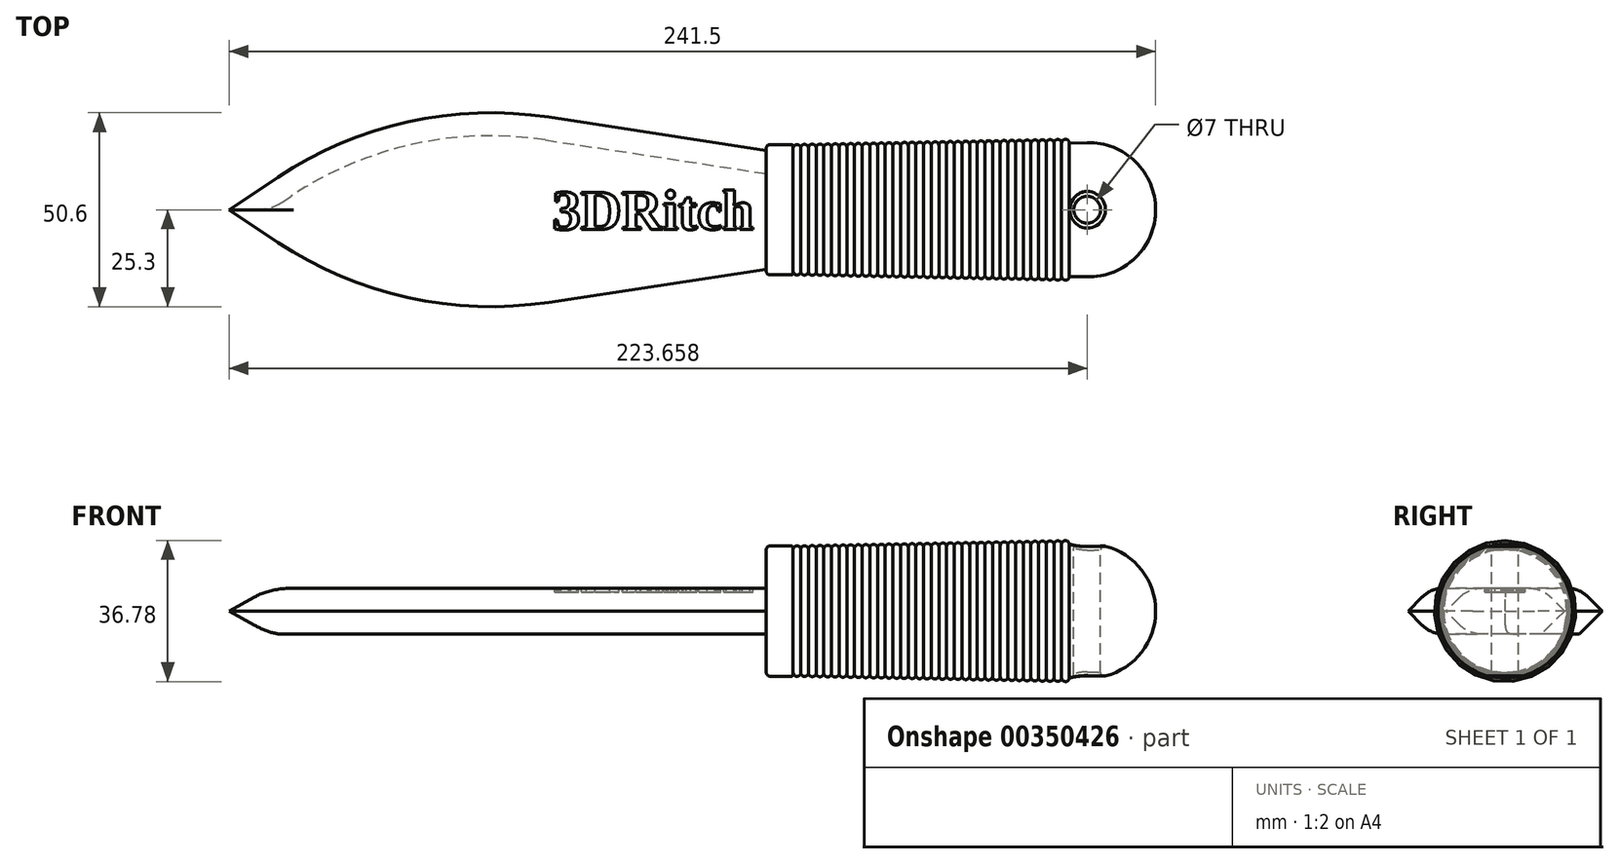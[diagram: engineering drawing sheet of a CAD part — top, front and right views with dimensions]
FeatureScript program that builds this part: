
annotation { "Feature Type Name" : "Feature", "Feature Type Description" : "" }
export const myFeature = defineFeature(function(context is Context, id is Id, definition is map)
    precondition{}
    {
        {
            var Q0;
            Q0=qCreatedBy(makeId("Top.planeOp"),FACE);
            var sketch = newSketch(context, id + "F0", { "sketchPlane" : qUnion([Q0])});
            skLineSegment(sketch, "E0", {"start": v(0, 0) * mm, "end": v(0, -16) * mm});
            skLineSegment(sketch, "E1", {"start": v(1, -17) * mm, "end": v(6.5, -17) * mm});
            skLineSegment(sketch, "E2", {"start": v(7, -16.5) * mm, "end": v(7, -16) * mm});
            skArc(sketch, "E3", {"start": v(83.66, -17.5) * mm, "mid": v(96.25, -12.5) * mm, "end": v(101.5, 0) * mm});
            skLineSegment(sketch, "E4", {"start": v(0, 0) * mm, "end": v(84, 0) * mm, "construction": true});
            skLineSegment(sketch, "E5", {"start": v(7, -16) * mm, "end": v(83.66, -17.5) * mm, "construction": true});
            skLineSegment(sketch, "E6", {"start": v(84, 0) * mm, "end": v(108.75, 0) * mm, "construction": true});
            skArc(sketch, "E7", {"start": v(7, -16) * mm, "mid": v(7.98, -17.02) * mm, "end": v(9, -16.04) * mm});
            skArc(sketch, "E8", {"start": v(9, -16.04) * mm, "mid": v(9.98, -17.06) * mm, "end": v(11, -16.08) * mm});
            skArc(sketch, "E9", {"start": v(13, -16.12) * mm, "mid": v(13.98, -17.14) * mm, "end": v(15, -16.16) * mm});
            skArc(sketch, "E10", {"start": v(15, -16.16) * mm, "mid": v(15.98, -17.18) * mm, "end": v(17, -16.2) * mm});
            skArc(sketch, "E11", {"start": v(17, -16.2) * mm, "mid": v(17.98, -17.21) * mm, "end": v(19, -16.23) * mm});
            skArc(sketch, "E12", {"start": v(19, -16.23) * mm, "mid": v(19.98, -17.25) * mm, "end": v(21, -16.27) * mm});
            skArc(sketch, "E13", {"start": v(21, -16.27) * mm, "mid": v(21.98, -17.3) * mm, "end": v(23, -16.31) * mm});
            skArc(sketch, "E14", {"start": v(11, -16.08) * mm, "mid": v(11.98, -17.1) * mm, "end": v(13, -16.12) * mm});
            skArc(sketch, "E15", {"start": v(23, -16.31) * mm, "mid": v(23.98, -17.33) * mm, "end": v(25, -16.35) * mm});
            skArc(sketch, "E16", {"start": v(25, -16.35) * mm, "mid": v(25.98, -17.37) * mm, "end": v(27, -16.4) * mm});
            skArc(sketch, "E17", {"start": v(27, -16.4) * mm, "mid": v(27.98, -17.4) * mm, "end": v(29, -16.43) * mm});
            skArc(sketch, "E18", {"start": v(31, -16.47) * mm, "mid": v(31.98, -17.49) * mm, "end": v(33, -16.5) * mm});
            skArc(sketch, "E19", {"start": v(35, -16.55) * mm, "mid": v(35.97, -17.57) * mm, "end": v(37, -16.59) * mm});
            skArc(sketch, "E20", {"start": v(37, -16.59) * mm, "mid": v(37.97, -17.6) * mm, "end": v(39, -16.62) * mm});
            skArc(sketch, "E21", {"start": v(39, -16.62) * mm, "mid": v(39.97, -17.64) * mm, "end": v(41, -16.66) * mm});
            skArc(sketch, "E22", {"start": v(41, -16.66) * mm, "mid": v(41.97, -17.68) * mm, "end": v(43, -16.7) * mm});
            skArc(sketch, "E23", {"start": v(43, -16.7) * mm, "mid": v(43.97, -17.72) * mm, "end": v(45, -16.74) * mm});
            skArc(sketch, "E24", {"start": v(29, -16.43) * mm, "mid": v(29.98, -17.45) * mm, "end": v(31, -16.47) * mm});
            skArc(sketch, "E25", {"start": v(33, -16.5) * mm, "mid": v(33.98, -17.53) * mm, "end": v(35, -16.55) * mm});
            skArc(sketch, "E26", {"start": v(45, -16.74) * mm, "mid": v(45.97, -17.76) * mm, "end": v(47, -16.78) * mm});
            skArc(sketch, "E27", {"start": v(47, -16.78) * mm, "mid": v(47.97, -17.8) * mm, "end": v(49, -16.82) * mm});
            skArc(sketch, "E28", {"start": v(49, -16.82) * mm, "mid": v(49.97, -17.84) * mm, "end": v(51, -16.86) * mm});
            skArc(sketch, "E29", {"start": v(51, -16.86) * mm, "mid": v(51.97, -17.88) * mm, "end": v(53, -16.9) * mm});
            skArc(sketch, "E30", {"start": v(53, -16.9) * mm, "mid": v(53.97, -17.92) * mm, "end": v(55, -16.94) * mm});
            skArc(sketch, "E31", {"start": v(55, -16.94) * mm, "mid": v(55.97, -17.96) * mm, "end": v(57, -16.98) * mm});
            skArc(sketch, "E32", {"start": v(57, -16.98) * mm, "mid": v(57.97, -18) * mm, "end": v(59, -17.02) * mm});
            skArc(sketch, "E33", {"start": v(59, -17.02) * mm, "mid": v(59.97, -18.03) * mm, "end": v(60.99, -17.05) * mm});
            skArc(sketch, "E34", {"start": v(60.99, -17.05) * mm, "mid": v(61.97, -18.07) * mm, "end": v(62.99, -17.1) * mm});
            skArc(sketch, "E35", {"start": v(62.99, -17.1) * mm, "mid": v(63.97, -18.11) * mm, "end": v(64.99, -17.13) * mm});
            skArc(sketch, "E36", {"start": v(64.99, -17.13) * mm, "mid": v(65.97, -18.15) * mm, "end": v(66.99, -17.17) * mm});
            skArc(sketch, "E37", {"start": v(66.99, -17.17) * mm, "mid": v(67.97, -18.2) * mm, "end": v(68.99, -17.21) * mm});
            skArc(sketch, "E38", {"start": v(68.99, -17.21) * mm, "mid": v(69.97, -18.23) * mm, "end": v(70.99, -17.25) * mm});
            skArc(sketch, "E39", {"start": v(70.99, -17.25) * mm, "mid": v(71.97, -18.27) * mm, "end": v(72.99, -17.29) * mm});
            skArc(sketch, "E40", {"start": v(72.99, -17.29) * mm, "mid": v(73.97, -18.3) * mm, "end": v(74.99, -17.33) * mm});
            skArc(sketch, "E41", {"start": v(74.99, -17.33) * mm, "mid": v(75.97, -18.35) * mm, "end": v(76.99, -17.37) * mm});
            skArc(sketch, "E42", {"start": v(76.99, -17.37) * mm, "mid": v(77.97, -18.39) * mm, "end": v(78.99, -17.4) * mm});
            skLineSegment(sketch, "E43", {"start": v(78.99, -17.4) * mm, "end": v(83.66, -17.5) * mm});
            skPoint(sketch, "E44.visualSharp", {"position": v(0, -17) * mm});
            skArc(sketch, "E44.filletArc", {"start": v(0, -16) * mm, "mid": v(0.3, -16.7) * mm, "end": v(1, -17) * mm});
            skPoint(sketch, "E45.visualSharp", {"position": v(7, -17) * mm});
            skArc(sketch, "E45.filletArc", {"start": v(6.5, -17) * mm, "mid": v(6.85, -16.85) * mm, "end": v(7, -16.5) * mm});
            skLineSegment(sketch, "E46", {"start": v(0, 0) * mm, "end": v(101.5, 0) * mm});
            skSolve(sketch);
        }
        {
            var Q0;
            Q0 = qSketchRegion(id + "F0", true);
            var Q1;
            Q1=sQuery(id+"F0.wireOp",EDGE,"E4");
            revolve(context, id + "F1", {"entities" : qUnion([Q0]), "axis" : qUnion([Q1]), "revolveType" : RevolveType.FULL});
        }
        {
            var Q0;
            Q0=qCreatedBy(makeId("Top.planeOp"),FACE);
            var sketch = newSketch(context, id + "F2", { "sketchPlane" : qUnion([Q0])});
            skLineSegment(sketch, "E47", {"start": v(0, 15.5) * mm, "end": v(0, -15.5) * mm});
            skLineSegment(sketch, "E48", {"start": v(0, 15.5) * mm, "end": v(-95, 30) * mm});
            skLineSegment(sketch, "E49", {"start": v(-95, 30) * mm, "end": v(-140, 0) * mm});
            skLineSegment(sketch, "E50", {"start": v(-140, 0) * mm, "end": v(-95, -30) * mm});
            skLineSegment(sketch, "E51", {"start": v(-95, -30) * mm, "end": v(0, -15.5) * mm});
            skLineSegment(sketch, "E52", {"start": v(-95, 30) * mm, "end": v(-95, 0) * mm, "construction": true});
            skLineSegment(sketch, "E53", {"start": v(-95, 0) * mm, "end": v(-95, -30) * mm, "construction": true});
            skSolve(sketch);
        }
        {
            var Q0;
            Q0 = qSketchRegion(id + "F2", true);
            extrude(context, id + "F3", {"entities" : qUnion([Q0]), "operationType" : NewBodyOperationType.ADD, "endBound" : BoundingType.SYMMETRIC, "depth" : 12 * mm});
        }
        {
            var Q0;
            Q0=makeQuery(id+"F3.opExtrude","SWEPT_EDGE",EDGE,{"disambiguationData":[OSD([sQuery(id+"F2.wireOp",EDGE,"E48"),sQuery(id+"F2.wireOp",EDGE,"E49")])]});
            var Q1;
            Q1=makeQuery(id+"F3.opExtrude","SWEPT_EDGE",EDGE,{"disambiguationData":[OSD([sQuery(id+"F2.wireOp",EDGE,"E50"),sQuery(id+"F2.wireOp",EDGE,"E51")])]});
            fillet(context, id + "F4", {"entities" : qUnion([Q0, Q1]), "radius" : 100 * mm, "tangentPropagation" : true, "allowEdgeOverflow" : false});
        }
        {
            var Q0;
            Q0=makeQuery(id+"F3.opExtrude","CAP_EDGE",EDGE,{"disambiguationData":[OSD([sQuery(id+"F2.wireOp",EDGE,"E49")])],"isStart":false});
            var Q1;
            Q1=makeQuery(id+"F3.opExtrude","CAP_EDGE",EDGE,{"disambiguationData":[OSD([sQuery(id+"F2.wireOp",EDGE,"E49")])],"isStart":true});
            var Q2;
            {var subQ0=sQuery(id+"F2.wireOp",EDGE,"E51");var subQ1=sQuery(id+"F2.wireOp",EDGE,"E50");Q2=makeQuery(id+"F4.opFillet","BLEND_EDGE",EDGE,{"blendedFrom":[makeQuery(id+"F3.opExtrude","SWEPT_EDGE",EDGE,{"disambiguationData":[OSD([subQ1,subQ0])]}),makeQuery(id+"F3.opExtrude","CAP_FACE",FACE,{"disambiguationData":[OSD([sQuery(id+"F2.wireOp",EDGE,"E47"),sQuery(id+"F2.wireOp",EDGE,"E48"),sQuery(id+"F2.wireOp",EDGE,"E49"),subQ1,subQ0])],"isStart":false})],"blendedInto":[makeQuery(id+"F3.opExtrude","CAP_FACE",FACE,{"disambiguationData":[OSD([sQuery(id+"F2.wireOp",EDGE,"E47"),sQuery(id+"F2.wireOp",EDGE,"E48"),sQuery(id+"F2.wireOp",EDGE,"E49"),subQ1,subQ0])],"isStart":false})]});}
            var Q3;
            {var subQ0=sQuery(id+"F2.wireOp",EDGE,"E51");var subQ1=sQuery(id+"F2.wireOp",EDGE,"E50");Q3=makeQuery(id+"F4.opFillet","BLEND_EDGE",EDGE,{"blendedFrom":[makeQuery(id+"F3.opExtrude","SWEPT_EDGE",EDGE,{"disambiguationData":[OSD([subQ1,subQ0])]}),makeQuery(id+"F3.opExtrude","CAP_FACE",FACE,{"disambiguationData":[OSD([sQuery(id+"F2.wireOp",EDGE,"E47"),sQuery(id+"F2.wireOp",EDGE,"E48"),sQuery(id+"F2.wireOp",EDGE,"E49"),subQ1,subQ0])],"isStart":true})],"blendedInto":[makeQuery(id+"F3.opExtrude","CAP_FACE",FACE,{"disambiguationData":[OSD([sQuery(id+"F2.wireOp",EDGE,"E47"),sQuery(id+"F2.wireOp",EDGE,"E48"),sQuery(id+"F2.wireOp",EDGE,"E49"),subQ1,subQ0])],"isStart":true})]});}
            chamfer(context, id + "F5", {"entities" : qUnion([Q0, Q1, Q2, Q3]), "chamferType" : ChamferType.OFFSET_ANGLE, "width" : 6 * mm, "oppositeDirection" : false, "angle" : 45 * degree, "tangentPropagation" : true});
        }
        {
            var Q0;
            {var subQ0=sQuery(id+"F2.wireOp",EDGE,"E48");Q0=makeQuery(id+"F5.opChamfer","BLEND_EDGE",EDGE,{"blendedFrom":[makeQuery(id+"F3.opExtrude","CAP_EDGE",EDGE,{"disambiguationData":[OSD([subQ0])],"isStart":false}),makeQuery(id+"F3.opExtrude","CAP_FACE",FACE,{"disambiguationData":[OSD([sQuery(id+"F2.wireOp",EDGE,"E47"),subQ0,sQuery(id+"F2.wireOp",EDGE,"E49"),sQuery(id+"F2.wireOp",EDGE,"E50"),sQuery(id+"F2.wireOp",EDGE,"E51")])],"isStart":false})],"blendedInto":[makeQuery(id+"F3.opExtrude","CAP_FACE",FACE,{"disambiguationData":[OSD([sQuery(id+"F2.wireOp",EDGE,"E47"),subQ0,sQuery(id+"F2.wireOp",EDGE,"E49"),sQuery(id+"F2.wireOp",EDGE,"E50"),sQuery(id+"F2.wireOp",EDGE,"E51")])],"isStart":false})]});}
            var Q1;
            {var subQ0=sQuery(id+"F2.wireOp",EDGE,"E51");var subQ1=sQuery(id+"F2.wireOp",EDGE,"E50");var subQ2=makeQuery(id+"F3.opExtrude","CAP_FACE",FACE,{"disambiguationData":[OSD([sQuery(id+"F2.wireOp",EDGE,"E47"),sQuery(id+"F2.wireOp",EDGE,"E48"),sQuery(id+"F2.wireOp",EDGE,"E49"),subQ1,subQ0])],"isStart":false});Q1=makeQuery(id+"F5.opChamfer","BLEND_EDGE",EDGE,{"blendedFrom":[makeQuery(id+"F4.opFillet","BLEND_EDGE",EDGE,{"blendedFrom":[makeQuery(id+"F3.opExtrude","SWEPT_EDGE",EDGE,{"disambiguationData":[OSD([subQ1,subQ0])]}),subQ2],"blendedInto":[subQ2]}),subQ2],"blendedInto":[subQ2]});}
            var Q2;
            {var subQ0=sQuery(id+"F2.wireOp",EDGE,"E51");Q2=makeQuery(id+"F5.opChamfer","BLEND_EDGE",EDGE,{"blendedFrom":[makeQuery(id+"F3.opExtrude","CAP_EDGE",EDGE,{"disambiguationData":[OSD([subQ0])],"isStart":false}),makeQuery(id+"F3.opExtrude","CAP_FACE",FACE,{"disambiguationData":[OSD([sQuery(id+"F2.wireOp",EDGE,"E47"),sQuery(id+"F2.wireOp",EDGE,"E48"),sQuery(id+"F2.wireOp",EDGE,"E49"),sQuery(id+"F2.wireOp",EDGE,"E50"),subQ0])],"isStart":false})],"blendedInto":[makeQuery(id+"F3.opExtrude","CAP_FACE",FACE,{"disambiguationData":[OSD([sQuery(id+"F2.wireOp",EDGE,"E47"),sQuery(id+"F2.wireOp",EDGE,"E48"),sQuery(id+"F2.wireOp",EDGE,"E49"),sQuery(id+"F2.wireOp",EDGE,"E50"),subQ0])],"isStart":false})]});}
            var Q3;
            {var subQ0=sQuery(id+"F2.wireOp",EDGE,"E51");var subQ1=sQuery(id+"F2.wireOp",EDGE,"E50");var subQ2=makeQuery(id+"F3.opExtrude","CAP_FACE",FACE,{"disambiguationData":[OSD([sQuery(id+"F2.wireOp",EDGE,"E47"),sQuery(id+"F2.wireOp",EDGE,"E48"),sQuery(id+"F2.wireOp",EDGE,"E49"),subQ1,subQ0])],"isStart":true});Q3=makeQuery(id+"F5.opChamfer","BLEND_EDGE",EDGE,{"blendedFrom":[makeQuery(id+"F4.opFillet","BLEND_EDGE",EDGE,{"blendedFrom":[makeQuery(id+"F3.opExtrude","SWEPT_EDGE",EDGE,{"disambiguationData":[OSD([subQ1,subQ0])]}),subQ2],"blendedInto":[subQ2]}),subQ2],"blendedInto":[subQ2]});}
            fillet(context, id + "F6", {"entities" : qUnion([Q0, Q1, Q2, Q3]), "radius" : 8 * mm, "tangentPropagation" : true, "allowEdgeOverflow" : false});
        }
        {
            var Q0;
            Q0=makeQuery(id+"F3.opExtrude","CAP_FACE",FACE,{"disambiguationData":[OSD([sQuery(id+"F2.wireOp",EDGE,"E47"),sQuery(id+"F2.wireOp",EDGE,"E48"),sQuery(id+"F2.wireOp",EDGE,"E49"),sQuery(id+"F2.wireOp",EDGE,"E50"),sQuery(id+"F2.wireOp",EDGE,"E51")])],"isStart":false});
            var sketch = newSketch(context, id + "F7", { "sketchPlane" : qUnion([Q0])});
            skText(sketch, "E54", { "text": "3DRitch", "fontName": "Tinos-Bold.ttf"});
            const initialGuessF7  = {"E54": [-0.05576, -0.00513, 1, 0, 0.01063]};
            skSetInitialGuess(sketch, initialGuessF7);
            skSolve(sketch);
        }
        {
            var Q0;
            Q0 = qSketchRegion(id + "F7", true);
            extrude(context, id + "F8", {"entities" : qUnion([Q0]), "operationType" : NewBodyOperationType.REMOVE, "oppositeDirection" : true, "depth" : 1 * mm});
        }
        {
            var Q0;
            Q0=qCreatedBy(makeId("Top.planeOp"),FACE);
            var sketch = newSketch(context, id + "F9", { "sketchPlane" : qUnion([Q0])});
            skCircle(sketch, "E55", {"center": v(83.66, 0) * mm, "radius": 3.5 * mm});
            skSolve(sketch);
        }
        {
            var Q0;
            Q0 = qSketchRegion(id + "F9", true);
            extrude(context, id + "F10", {"entities" : qUnion([Q0]), "operationType" : NewBodyOperationType.REMOVE, "endBound" : BoundingType.SYMMETRIC, "oppositeDirection" : true, "depth" : 100 * mm});
        }
        {
            var Q0;
            Q0=makeQuery(id+"F10.boolean.opBoolean","INTERSECT",EDGE,{"disambiguationData":[OD(1.0)],"derivedFrom":[makeQuery(id+"F1.opRevolve","SWEPT_FACE",FACE,{"disambiguationData":[OSD([sQuery(id+"F0.wireOp",EDGE,"E43")])]}),makeQuery(id+"F10.opExtrude","SWEPT_FACE",FACE,{"disambiguationData":[OSD([sQuery(id+"F9.wireOp",EDGE,"E55")])]})]});
            var Q1;
            Q1=makeQuery(id+"F10.boolean.opBoolean","INTERSECT",EDGE,{"disambiguationData":[OD(0.0)],"derivedFrom":[makeQuery(id+"F1.opRevolve","SWEPT_FACE",FACE,{"disambiguationData":[OSD([sQuery(id+"F0.wireOp",EDGE,"E3")])]}),makeQuery(id+"F10.opExtrude","SWEPT_FACE",FACE,{"disambiguationData":[OSD([sQuery(id+"F9.wireOp",EDGE,"E55")])]})]});
            var Q2;
            Q2=makeQuery(id+"F10.boolean.opBoolean","INTERSECT",EDGE,{"disambiguationData":[OD(0.0)],"derivedFrom":[makeQuery(id+"F1.opRevolve","SWEPT_FACE",FACE,{"disambiguationData":[OSD([sQuery(id+"F0.wireOp",EDGE,"E43")])]}),makeQuery(id+"F10.opExtrude","SWEPT_FACE",FACE,{"disambiguationData":[OSD([sQuery(id+"F9.wireOp",EDGE,"E55")])]})]});
            fillet(context, id + "F11", {"entities" : qUnion([Q0, Q1, Q2]), "radius" : 1 * mm, "tangentPropagation" : true, "allowEdgeOverflow" : false});
        }
    });
